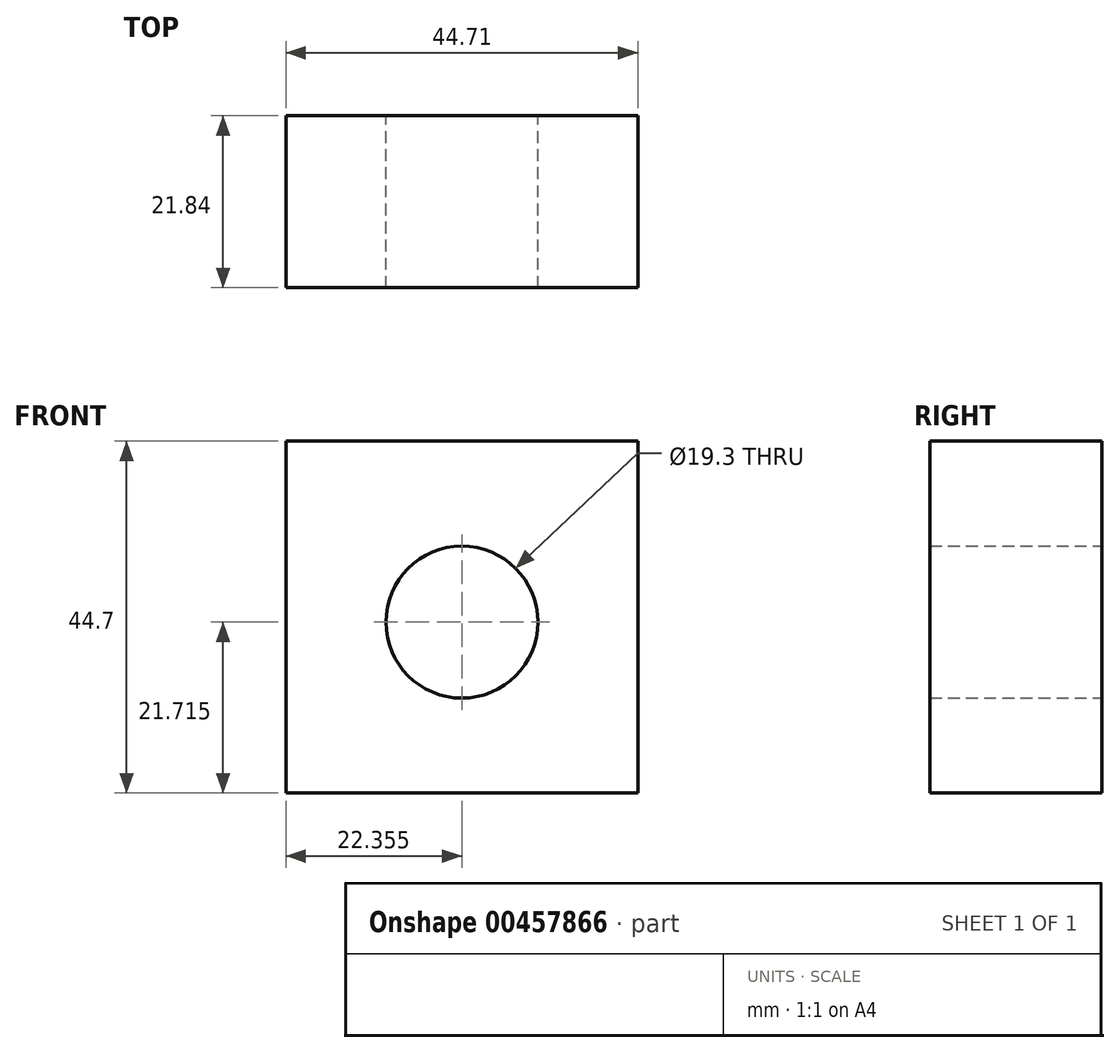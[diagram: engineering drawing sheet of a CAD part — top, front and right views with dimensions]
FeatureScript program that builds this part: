
annotation { "Feature Type Name" : "Feature", "Feature Type Description" : "" }
export const myFeature = defineFeature(function(context is Context, id is Id, definition is map)
    precondition{}
    {
        {
            var Q0;
            Q0=qCreatedBy(makeId("Front.planeOp"),FACE);
            var sketch = newSketch(context, id + "F0", { "sketchPlane" : qUnion([Q0])});
            skLineSegment(sketch, "E0.bottom", {"start": v(-39.48, 25.91) * mm, "end": v(5.23, 25.91) * mm});
            skLineSegment(sketch, "E0.top", {"start": v(-39.48, -18.8) * mm, "end": v(5.23, -18.8) * mm});
            skLineSegment(sketch, "E0.left", {"start": v(-39.48, 25.91) * mm, "end": v(-39.48, -18.8) * mm});
            skCircle(sketch, "E1", {"center": v(-17.13, 2.92) * mm, "radius": 9.65 * mm});
            skPoint(sketch, "E2.orphan", {"position": v(5.23, 25.91) * mm});
            skLineSegment(sketch, "E3", {"start": v(5.23, 25.91) * mm, "end": v(5.23, -18.8) * mm});
            skSolve(sketch);
        }
        {
            var Q0;
            Q0=qSketchRegion(id+"F0",true);
            extrude(context, id + "F1", {"entities" : qUnion([Q0]), "depth" : 21.84 * mm});
        }
    });
